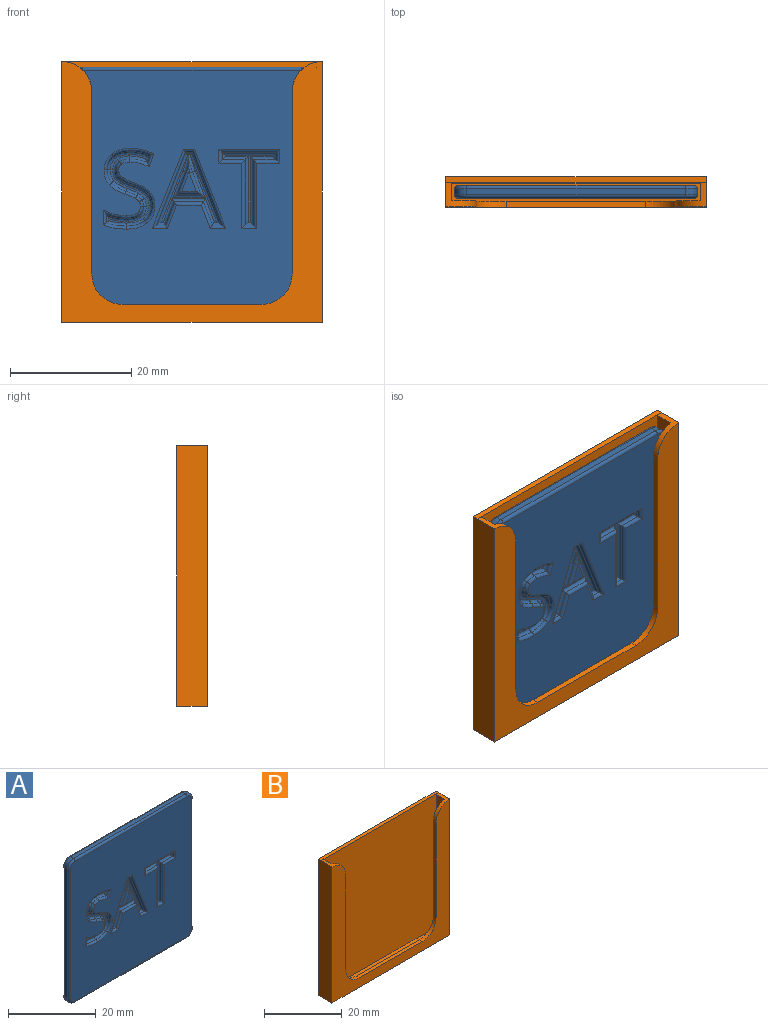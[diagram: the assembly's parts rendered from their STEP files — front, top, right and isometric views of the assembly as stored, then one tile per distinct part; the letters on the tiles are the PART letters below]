
ASSEMBLY  parts=2 mates=1
PART A: 122 faces, bbox 40.3x2x40.3 mm
  f0: plane 39x39mm, normal (0,-1,0), area 1341.3mm2, adj f26,f29,f30,f33,f34,f37,f38,f39
  f1: cylinder r=2mm len=2mm, axis (0,1,0), area 3.1mm2, adj f2,f8,f110,f118
  f2: plane 36x1mm, normal (0,0,1), area 36mm2, adj f1,f3,f108,f116
  f3: cylinder r=2mm len=2mm, axis (0,1,0), area 3.1mm2, adj f2,f4,f106,f114
  f4: plane 36x1mm, normal (-1,0,0), area 36mm2, adj f3,f5,f107,f115
  f5: cylinder r=2mm len=2mm, axis (0,1,0), area 3.1mm2, adj f4,f6,f109,f117
  f6: plane 36x1mm, normal (0,0,-1), area 36mm2, adj f5,f7,f111,f119
  f7: cylinder r=2mm len=2mm, axis (0,1,0), area 3.1mm2, adj f6,f8,f113,f121
  f8: plane 36x1mm, normal (1,0,0), area 36mm2, adj f1,f7,f112,f120
  f9: plane 39x39mm, normal (0,1,0), area 1519.1mm2, adj f106,f107,f108,f109,f110,f111,f112,f113
  f10: plane 11.01x9.14mm, normal (0,-1,0), area 7.4mm2, adj f16,f19,f20,f22,f23,f24,f25,f27
  f11: plane 3.22x2.42mm, normal (0,-1,0), area 3.9mm2, adj f14,f15,f17,f18,f21
  f12: plane 10.96x7.97mm, normal (0,-1,0), area 6.1mm2, adj f40,f41,f43,f44,f47,f48,f51,f52
  f13: plane 11.3x6.53mm, normal (0,-1,0), area 7.7mm2, adj f56,f57,f58,f61,f62,f65,f66,f69
  f14: cylinder r=0.5mm len=3.88mm, axis (-0.35,0,0.94), area 2.8mm2, adj f11,f15,f16,f17
  f15: cylinder r=0.5mm len=3.87mm, axis (1,0,0), area 2.5mm2, adj f11,f14,f18,f19
  f16: cylinder r=0.5mm len=4.56mm, axis (0.35,0,-0.94), area 3.4mm2, adj f10,f14,f19,f20
  f17: bspline ~2.37x1.2mm, area 0.9mm2, adj f11,f14,f20,f21
  f18: cylinder r=0.5mm len=3.89mm, axis (-0.35,0,-0.94), area 2.8mm2, adj f11,f15,f21,f22
  f19: cylinder r=0.5mm len=5.32mm, axis (-1,0,0), area 3.6mm2, adj f10,f15,f16,f22
  f20: bspline ~3.99x1.65mm, area 2mm2, adj f10,f16,f17,f23,f24
  f21: bspline ~2.66x1.23mm, area 0.9mm2, adj f11,f17,f18,f24
  f22: cylinder r=0.5mm len=4.56mm, axis (0.35,0,0.94), area 3.4mm2, adj f10,f18,f19,f24
  f23: cylinder r=0.5mm len=1.17mm, axis (-1,0,0), area 0.7mm2, adj f10,f20,f24,f25,f26,f27
  f24: bspline ~3.46x1.37mm, area 2mm2, adj f10,f20,f21,f22,f23,f27
  f25: cylinder r=0.5mm len=12.19mm, axis (-0.36,0,0.93), area 9.7mm2, adj f10,f23,f28,f29
  f26: cylinder r=0.5mm len=1.85mm, axis (1,0,0), area 1.2mm2, adj f0,f23,f29,f30
  f27: cylinder r=0.5mm len=12.19mm, axis (-0.37,0,-0.93), area 9.7mm2, adj f10,f23,f24,f30,f31
  f28: cylinder r=0.5mm len=1.44mm, axis (1,0,0), area 0.7mm2, adj f10,f25,f32,f33
  f29: cylinder r=0.5mm len=13.19mm, axis (0.36,0,-0.93), area 10.6mm2, adj f0,f25,f26,f33
  f30: cylinder r=0.5mm len=13.19mm, axis (0.37,0,0.93), area 10.6mm2, adj f0,f26,f27,f34
  f31: cylinder r=0.5mm len=1.41mm, axis (1,0,0), area 0.7mm2, adj f10,f27,f34,f35
  f32: cylinder r=0.5mm len=4.3mm, axis (0.36,0,-0.93), area 3.2mm2, adj f10,f28,f36,f37
  f33: cylinder r=0.5mm len=2.51mm, axis (-1,0,0), area 1.6mm2, adj f0,f28,f29,f37
  f34: cylinder r=0.5mm len=2.49mm, axis (-1,0,0), area 1.5mm2, adj f0,f30,f31,f38
  f35: cylinder r=0.5mm len=4.3mm, axis (0.36,0,0.93), area 3.2mm2, adj f10,f31,f36,f38
  f36: cylinder r=0.5mm len=5.48mm, axis (1,0,0), area 4mm2, adj f10,f32,f35,f39
  f37: cylinder r=0.5mm len=4.3mm, axis (-0.36,0,0.93), area 3.2mm2, adj f0,f32,f33,f39
  f38: cylinder r=0.5mm len=4.3mm, axis (-0.36,0,-0.93), area 3.2mm2, adj f0,f34,f35,f39
  f39: cylinder r=0.5mm len=4.79mm, axis (-1,0,0), area 3.5mm2, adj f0,f36,f37,f38
  f40: cylinder r=0.5mm len=1.24mm, axis (0,0,1), area 0.6mm2, adj f12,f41,f42,f43
  f41: cylinder r=0.5mm len=4.29mm, axis (1,0,0), area 3mm2, adj f12,f40,f44,f45
  f42: cylinder r=0.5mm len=2.24mm, axis (0,0,-1), area 1.4mm2, adj f0,f40,f45,f46
  f43: cylinder r=0.5mm len=8.97mm, axis (-1,0,0), area 6.6mm2, adj f12,f40,f46,f47
  f44: cylinder r=0.5mm len=11.23mm, axis (0,0,1), area 8.4mm2, adj f12,f41,f48,f49
  f45: cylinder r=0.5mm len=4.29mm, axis (-1,0,0), area 3mm2, adj f0,f41,f42,f49
  f46: cylinder r=0.5mm len=9.97mm, axis (1,0,0), area 7.4mm2, adj f0,f42,f43,f50
  f47: cylinder r=0.5mm len=1.24mm, axis (0,0,-1), area 0.6mm2, adj f12,f43,f50,f51
  f48: cylinder r=0.5mm len=1.39mm, axis (1,0,0), area 0.7mm2, adj f12,f44,f52,f53
  f49: cylinder r=0.5mm len=11.23mm, axis (0,0,-1), area 8.4mm2, adj f0,f44,f45,f53
  f50: cylinder r=0.5mm len=2.24mm, axis (0,0,1), area 1.4mm2, adj f0,f46,f47,f54
  f51: cylinder r=0.5mm len=4.29mm, axis (1,0,0), area 3mm2, adj f12,f47,f52,f54
  f52: cylinder r=0.5mm len=11.23mm, axis (0,0,-1), area 8.4mm2, adj f12,f48,f51,f55
  f53: cylinder r=0.5mm len=2.39mm, axis (-1,0,0), area 1.5mm2, adj f0,f48,f49,f55
  f54: cylinder r=0.5mm len=4.29mm, axis (-1,0,0), area 3mm2, adj f0,f50,f51,f55
  f55: cylinder r=0.5mm len=11.23mm, axis (0,0,1), area 8.4mm2, adj f0,f52,f53,f54
  f56: bspline ~3.58x2.44mm, area 2.1mm2, adj f13,f57,f58,f59
  f57: bspline ~2.82x1.6mm, area 1.5mm2, adj f13,f56,f60,f61
  f58: bspline ~3.29x1.37mm, area 1.7mm2, adj f13,f56,f62,f63
  f59: bspline ~3.79x2.59mm, area 2.3mm2, adj f0,f56,f60,f63
  f60: bspline ~2.74x1.56mm, area 1.5mm2, adj f0,f57,f59,f64
  f61: bspline ~1.64x1.53mm, area 1mm2, adj f13,f57,f64,f65
  f62: bspline ~3.28x1.87mm, area 1.9mm2, adj f13,f58,f66,f67
  f63: bspline ~3.62x1.49mm, area 1.9mm2, adj f0,f58,f59,f67
  f64: bspline ~1.47x1.37mm, area 0.8mm2, adj f0,f60,f61,f68
  f65: bspline ~1.7x0.87mm, area 0.9mm2, adj f13,f61,f68,f69
  f66: bspline ~3.4x1.59mm, area 2.2mm2, adj f13,f62,f70,f71
  f67: bspline ~3.68x2.06mm, area 2.1mm2, adj f0,f62,f63,f71
  f68: bspline ~1.43x0.79mm, area 0.8mm2, adj f0,f64,f65,f72
  f69: bspline ~2.19x1.51mm, area 1.5mm2, adj f13,f65,f72,f73
  f70: bspline ~4.13x1.21mm, area 2.4mm2, adj f13,f66,f74,f75
  f71: bspline ~4.17x1.7mm, area 2.4mm2, adj f0,f66,f67,f75
  f72: bspline ~1.8x1.31mm, area 1.2mm2, adj f0,f68,f69,f76
  f73: bspline ~3.27x1.32mm, area 1.8mm2, adj f13,f69,f76,f77
  f74: cylinder r=0.5mm len=1.38mm, axis (0.34,0,0.94), area 0.6mm2, adj f13,f70,f78,f79
  f75: bspline ~6.79x2.25mm, area 2.9mm2, adj f0,f70,f71,f79
  f76: bspline ~2.98x1.22mm, area 1.6mm2, adj f0,f72,f73,f80
  f77: bspline ~2.44x0.74mm, area 1.4mm2, adj f13,f73,f80,f81
  f78: bspline ~4.42x1.45mm, area 2.2mm2, adj f13,f74,f82,f83
  f79: cylinder r=0.5mm len=2.31mm, axis (-0.34,0,-0.94), area 1.4mm2, adj f0,f74,f75,f83
  f80: bspline ~2.34x0.73mm, area 1.3mm2, adj f0,f76,f77,f84
  f81: bspline ~2.48x1.2mm, area 1.1mm2, adj f13,f77,f84,f85
  f82: bspline ~2.7x1.2mm, area 1.5mm2, adj f13,f78,f86,f87
  f83: bspline ~4.74x1.56mm, area 2.5mm2, adj f0,f78,f79,f87
  f84: bspline ~3.5x1.62mm, area 1.6mm2, adj f0,f80,f81,f88
  f85: cylinder r=0.5mm len=1.34mm, axis (0,0,-1), area 0.6mm2, adj f13,f81,f88,f89
  f86: bspline ~2.32x1.42mm, area 1.3mm2, adj f13,f82,f90,f91
  f87: bspline ~2.4x1.1mm, area 1.3mm2, adj f0,f82,f83,f91
  f88: cylinder r=0.5mm len=2.41mm, axis (0,0,1), area 1.5mm2, adj f0,f84,f85,f92
  f89: bspline ~4.62x1.29mm, area 2.4mm2, adj f13,f85,f92,f93
  f90: bspline ~1.73x0.85mm, area 0.9mm2, adj f13,f86,f94,f95
  f91: bspline ~1.71x1.28mm, area 1.1mm2, adj f0,f86,f87,f95
  f92: bspline ~4.79x1.22mm, area 2.8mm2, adj f0,f88,f89,f96
  f93: bspline ~4.4x1.72mm, area 2.5mm2, adj f13,f89,f96,f97
  f94: bspline ~1.46x1.34mm, area 0.9mm2, adj f13,f90,f98,f99
  f95: bspline ~1.49x0.79mm, area 0.8mm2, adj f0,f90,f91,f99
  f96: bspline ~4.71x1.83mm, area 2.7mm2, adj f0,f92,f93,f100
  f97: bspline ~3.68x2.05mm, area 2.1mm2, adj f13,f93,f100,f101
  f98: bspline ~2.67x1.56mm, area 1.5mm2, adj f13,f94,f102,f103
  f99: bspline ~1.24x1.22mm, area 0.8mm2, adj f0,f94,f95,f103
  f100: bspline ~3.73x1.79mm, area 2.3mm2, adj f0,f96,f97,f104
  f101: bspline ~2.47x1.33mm, area 1.6mm2, adj f13,f97,f102,f104
  f102: bspline ~3.67x2.28mm, area 2.3mm2, adj f13,f98,f101,f105
  f103: bspline ~2.29x1.41mm, area 1.4mm2, adj f0,f98,f99,f105
  f104: bspline ~3.35x1.46mm, area 1.8mm2, adj f0,f100,f101,f105
  f105: bspline ~3.87x2.41mm, area 2.4mm2, adj f0,f102,f103,f104
  f106: torus R=1.5mm, axis (0,-1,0), area 2.2mm2, adj f3,f9,f107,f108
  f107: cylinder r=0.5mm len=36mm, axis (0,0,-1), area 28.3mm2, adj f4,f9,f106,f109
  f108: cylinder r=0.5mm len=36mm, axis (-1,0,0), area 28.3mm2, adj f2,f9,f106,f110
  f109: torus R=1.5mm, axis (0,-1,0), area 2.2mm2, adj f5,f9,f107,f111
  f110: torus R=1.5mm, axis (0,-1,0), area 2.2mm2, adj f1,f9,f108,f112
  f111: cylinder r=0.5mm len=36mm, axis (1,0,0), area 28.3mm2, adj f6,f9,f109,f113
  f112: cylinder r=0.5mm len=36mm, axis (0,0,1), area 28.3mm2, adj f8,f9,f110,f113
  f113: torus R=1.5mm, axis (0,-1,0), area 2.2mm2, adj f7,f9,f111,f112
  f114: torus R=1.5mm, axis (0,-1,0), area 2.2mm2, adj f0,f3,f115,f116
  f115: cylinder r=0.5mm len=36mm, axis (0,0,1), area 28.3mm2, adj f0,f4,f114,f117
  f116: cylinder r=0.5mm len=36mm, axis (1,0,0), area 28.3mm2, adj f0,f2,f114,f118
  f117: torus R=1.5mm, axis (0,-1,0), area 2.2mm2, adj f0,f5,f115,f119
  f118: torus R=1.5mm, axis (0,-1,0), area 2.2mm2, adj f0,f1,f116,f120
  f119: cylinder r=0.5mm len=36mm, axis (-1,0,0), area 28.3mm2, adj f0,f6,f117,f121
  f120: cylinder r=0.5mm len=36mm, axis (0,0,-1), area 28.3mm2, adj f0,f8,f118,f121
  f121: torus R=1.5mm, axis (0,-1,0), area 2.2mm2, adj f0,f7,f119,f120
PART B: 18 faces, bbox 43x5x43 mm
  f0: plane 43x43mm, normal (0,-1,0), area 529mm2, adj f5,f6,f7,f11,f12,f13,f14,f15
  f1: plane 41.9x3mm, normal (-1,0,0), area 125.7mm2, adj f3,f9,f10,f17
  f2: plane 41.9x3mm, normal (1,0,0), area 125.7mm2, adj f3,f9,f10,f11
  f3: plane 41.9x41mm, normal (0,1,0), area 402.1mm2, adj f1,f2,f9,f11,f12,f13,f14,f15
  f4: plane 43x1mm, normal (0,0,1), area 43mm2, adj f5,f6,f8,f10
  f5: plane 43x5mm, normal (1,0,0), area 215mm2, adj f0,f4,f7,f8,f17
  f6: plane 43x5mm, normal (-1,0,0), area 215mm2, adj f0,f4,f7,f8,f11
  f7: plane 43x5mm, normal (0,0,-1), area 215mm2, adj f0,f5,f6,f8
  f8: plane 43x43mm, normal (0,1,0), area 1849mm2, adj f4,f5,f6,f7
  f9: plane 41x3mm, normal (0,0,1), area 123mm2, adj f1,f2,f3,f10
  f10: plane 43x42mm, normal (0,-1,0), area 1722.1mm2, adj f1,f2,f4,f9,f11,f17
  f11: cylinder r=5mm len=5mm, axis (0,-1,0), area 10.9mm2, adj f0,f2,f3,f6,f10,f12
  f12: plane 30x1mm, normal (1,0,0), area 30mm2, adj f0,f3,f11,f13
  f13: cylinder r=5mm len=5mm, axis (0,-1,0), area 7.9mm2, adj f0,f3,f12,f14
  f14: plane 23x1mm, normal (0,0,1), area 23mm2, adj f0,f3,f13,f15
  f15: cylinder r=5mm len=5mm, axis (0,-1,0), area 7.9mm2, adj f0,f3,f14,f16
  f16: plane 30x1mm, normal (-1,0,0), area 30mm2, adj f0,f3,f15,f17
  f17: cylinder r=5mm len=5mm, axis (0,-1,0), area 10.9mm2, adj f0,f1,f3,f5,f10,f16
PLACE A t=(0,-1.5,0.58)mm
PLACE B at identity fixed
MATE slider A.f2 <-> B.f9  axis (0,0,1) through (0,-2.5,20.58)mm
